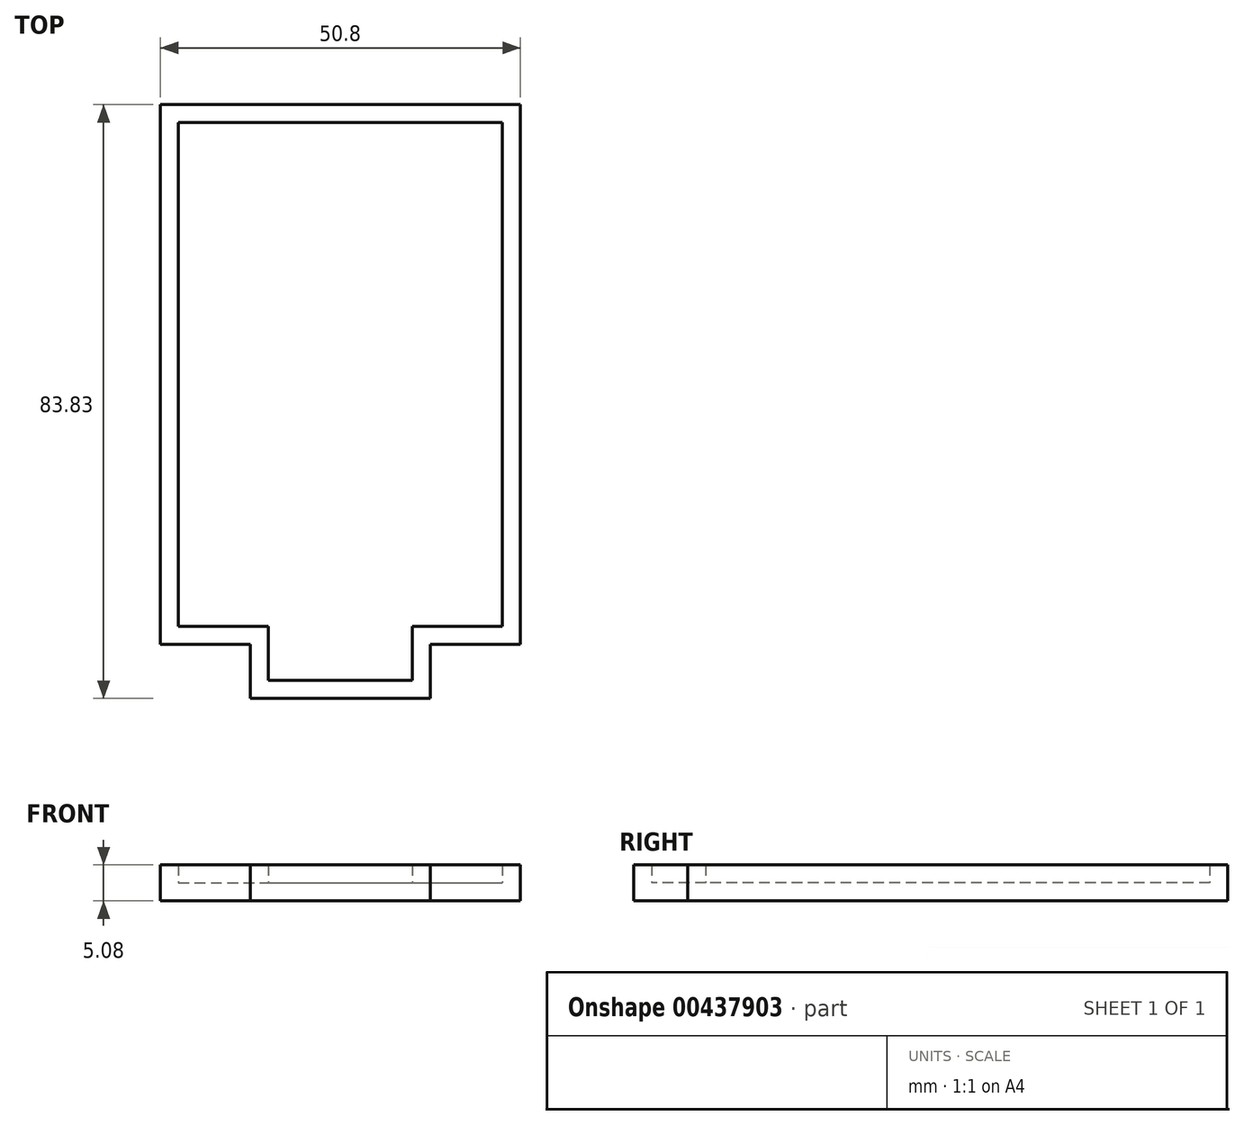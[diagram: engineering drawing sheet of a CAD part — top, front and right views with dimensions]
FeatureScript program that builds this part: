
annotation { "Feature Type Name" : "Feature", "Feature Type Description" : "" }
export const myFeature = defineFeature(function(context is Context, id is Id, definition is map)
    precondition{}
    {
        {
            var Q0;
            Q0=qCreatedBy(makeId("Top.planeOp"),FACE);
            var sketch = newSketch(context, id + "F0", { "sketchPlane" : qUnion([Q0])});
            skLineSegment(sketch, "E0.bottom", {"start": v(-58.52, 45.03) * mm, "end": v(-7.72, 45.03) * mm});
            skLineSegment(sketch, "E0.top", {"start": v(-58.52, -31.17) * mm, "end": v(-7.72, -31.17) * mm});
            skLineSegment(sketch, "E0.left", {"start": v(-58.52, 45.03) * mm, "end": v(-58.52, -31.17) * mm});
            skLineSegment(sketch, "E0.right", {"start": v(-7.72, 45.03) * mm, "end": v(-7.72, -31.17) * mm});
            skLineSegment(sketch, "E1.top", {"start": v(-45.82, -38.8) * mm, "end": v(-20.42, -38.8) * mm});
            skLineSegment(sketch, "E1.left", {"start": v(-45.82, -31.17) * mm, "end": v(-45.82, -38.8) * mm});
            skLineSegment(sketch, "E1.right", {"start": v(-20.42, -31.17) * mm, "end": v(-20.42, -38.8) * mm});
            skSolve(sketch);
        }
        {
            var Q0;
            Q0=makeQuery(id+"F0.imprint","IMPRINT",FACE,{"disambiguationData":[TD([[makeQuery(id+"F0.imprint","IMPRINT",EDGE,{"derivedFrom":sQuery(id+"F0.wireOp",EDGE,"E0.bottom")}),-1.0]])]});
            var Q1;
            Q1=makeQuery(id+"F0.imprint","IMPRINT",FACE,{"disambiguationData":[TD([[makeQuery(id+"F0.imprint","IMPRINT",EDGE,{"derivedFrom":sQuery(id+"F0.wireOp",EDGE,"E1.top")}),1.0]])]});
            extrude(context, id + "F1", {"entities" : qUnion([Q0, Q1]), "depth" : 5.08 * mm});
        }
        {
            var Q0;
            Q0=makeQuery(id+"F1.opExtrude","CAP_FACE",FACE,{"disambiguationData":[OSD([sQuery(id+"F0.wireOp",EDGE,"E0.bottom"),sQuery(id+"F0.wireOp",EDGE,"E0.top"),sQuery(id+"F0.wireOp",EDGE,"E0.left"),sQuery(id+"F0.wireOp",EDGE,"E0.right")])],"isStart":false});
            shell(context, id + "F2", {"entities" : qUnion([Q0]), "thickness" : 2.54 * mm});
        }
    });
